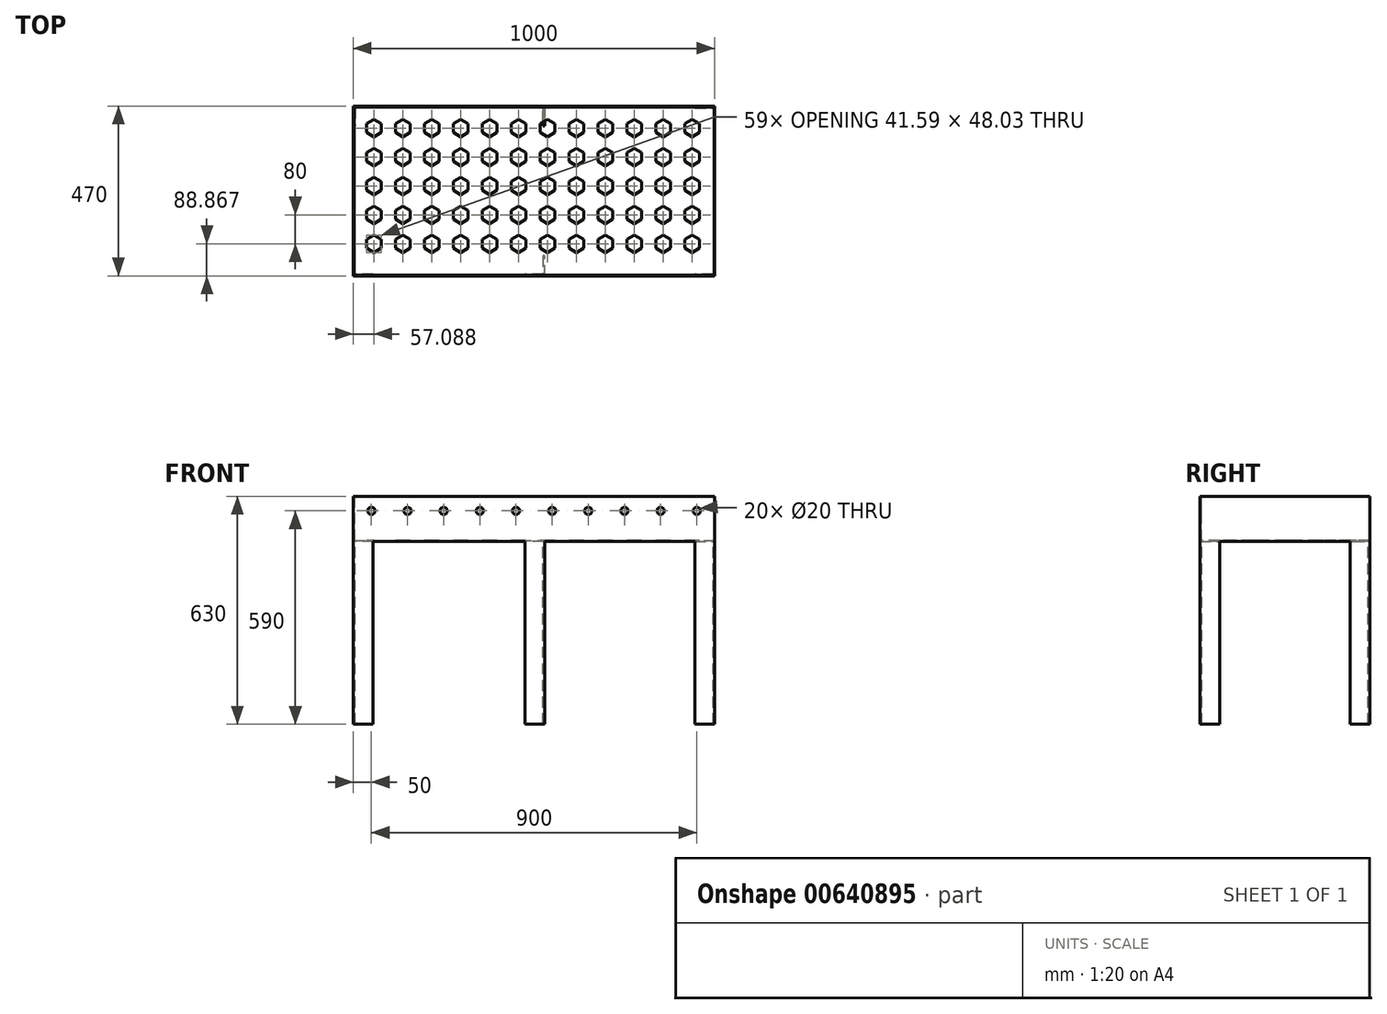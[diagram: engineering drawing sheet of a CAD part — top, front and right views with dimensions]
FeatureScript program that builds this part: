
annotation { "Feature Type Name" : "Feature", "Feature Type Description" : "" }
export const myFeature = defineFeature(function(context is Context, id is Id, definition is map)
    precondition{}
    {
        {
            var Q0;
            Q0=qCreatedBy(makeId("Top.planeOp"),FACE);
            cPlane(context, id + "F0", {"entities" : qUnion([Q0]), "cplaneType" : CPlaneType.OFFSET, "offset" : 505 * mm, "width" : 152.4 * mm, "height" : 152.4 * mm});
        }
        {
            var Q0;
            Q0=qCreatedBy(id+"F0.planeOp",FACE);
            var sketch = newSketch(context, id + "F1", { "sketchPlane" : qUnion([Q0])});
            skLineSegment(sketch, "E0", {"start": v(0, 1050.52) * mm, "end": v(0, -1050.52) * mm, "construction": true});
            skLineSegment(sketch, "E1", {"start": v(-920.74, 0) * mm, "end": v(994.2, 0) * mm, "construction": true});
            skLineSegment(sketch, "E2.bottom", {"start": v(-500, 235) * mm, "end": v(500, 235) * mm});
            skLineSegment(sketch, "E2.top", {"start": v(-500, -235) * mm, "end": v(500, -235) * mm});
            skLineSegment(sketch, "E2.left", {"start": v(-500, 235) * mm, "end": v(-500, -235) * mm});
            skLineSegment(sketch, "E2.right", {"start": v(500, 235) * mm, "end": v(500, -235) * mm});
            skSolve(sketch);
        }
        {
            var Q0;
            Q0=makeQuery(id+"F1.imprint","IMPRINT",FACE,{"disambiguationData":[TD([[makeQuery(id+"F1.imprint","IMPRINT",EDGE,{"derivedFrom":sQuery(id+"F1.wireOp",EDGE,"E2.bottom")}),-1.0]])]});
            extrude(context, id + "F2", {"entities" : qUnion([Q0]), "depth" : 125 * mm, "offsetDistance" : 25.4 * mm});
        }
        {
            var Q0;
            Q0=makeQuery(id+"F2.opExtrude","CAP_FACE",FACE,{"disambiguationData":[OSD([sQuery(id+"F1.wireOp",EDGE,"E2.bottom"),sQuery(id+"F1.wireOp",EDGE,"E2.top"),sQuery(id+"F1.wireOp",EDGE,"E2.left"),sQuery(id+"F1.wireOp",EDGE,"E2.right")])],"isStart":false});
            shell(context, id + "F3", {"entities" : qUnion([Q0]), "thickness" : 2.54 * mm});
        }
        {
            var Q0;
            Q0=makeQuery(id+"F2.opExtrude","CAP_FACE",FACE,{"disambiguationData":[OSD([sQuery(id+"F1.wireOp",EDGE,"E2.bottom"),sQuery(id+"F1.wireOp",EDGE,"E2.top"),sQuery(id+"F1.wireOp",EDGE,"E2.left"),sQuery(id+"F1.wireOp",EDGE,"E2.right")])],"isStart":true});
            var sketch = newSketch(context, id + "F4", { "sketchPlane" : qUnion([Q0])});
            skLineSegment(sketch, "E3", {"start": v(445, 235) * mm, "end": v(500, 235) * mm});
            skLineSegment(sketch, "E4", {"start": v(500, 235) * mm, "end": v(500, 180) * mm});
            skLineSegment(sketch, "E5", {"start": v(500, 180) * mm, "end": v(495, 180) * mm});
            skLineSegment(sketch, "E6", {"start": v(495, 180) * mm, "end": v(495, 230) * mm});
            skLineSegment(sketch, "E7", {"start": v(495, 230) * mm, "end": v(445, 230) * mm});
            skLineSegment(sketch, "E8", {"start": v(445, 230) * mm, "end": v(445, 235) * mm});
            skLineSegment(sketch, "E9", {"start": v(500, -180) * mm, "end": v(500, -235) * mm});
            skLineSegment(sketch, "E10", {"start": v(500, -235) * mm, "end": v(445, -235) * mm});
            skLineSegment(sketch, "E11", {"start": v(445, -235) * mm, "end": v(445, -230) * mm});
            skLineSegment(sketch, "E12", {"start": v(445, -230) * mm, "end": v(495, -230) * mm});
            skLineSegment(sketch, "E13", {"start": v(495, -230) * mm, "end": v(495, -180) * mm});
            skLineSegment(sketch, "E14", {"start": v(495, -180) * mm, "end": v(500, -180) * mm});
            skLineSegment(sketch, "E15", {"start": v(0, 297.82) * mm, "end": v(0, -372.57) * mm, "construction": true});
            skLineSegment(sketch, "E16", {"start": v(-25, 235) * mm, "end": v(30, 235) * mm});
            skLineSegment(sketch, "E17", {"start": v(30, 235) * mm, "end": v(30, 180) * mm});
            skLineSegment(sketch, "E18", {"start": v(30, 180) * mm, "end": v(25, 180) * mm});
            skLineSegment(sketch, "E19", {"start": v(25, 180) * mm, "end": v(25, 230) * mm});
            skLineSegment(sketch, "E20", {"start": v(25, 230) * mm, "end": v(-25, 230) * mm});
            skLineSegment(sketch, "E21", {"start": v(-25, 230) * mm, "end": v(-25, 235) * mm});
            skLineSegment(sketch, "E22", {"start": v(-25, -235) * mm, "end": v(30, -235) * mm});
            skLineSegment(sketch, "E23", {"start": v(30, -235) * mm, "end": v(30, -180) * mm});
            skLineSegment(sketch, "E24", {"start": v(30, -180) * mm, "end": v(25, -180) * mm});
            skLineSegment(sketch, "E25", {"start": v(25, -180) * mm, "end": v(25, -230) * mm});
            skLineSegment(sketch, "E26", {"start": v(25, -230) * mm, "end": v(-25, -230) * mm});
            skLineSegment(sketch, "E27", {"start": v(-25, -230) * mm, "end": v(-25, -235) * mm});
            skLineSegment(sketch, "E28", {"start": v(-500, 180) * mm, "end": v(-500, 235) * mm});
            skLineSegment(sketch, "E29", {"start": v(-500, 235) * mm, "end": v(-445, 235) * mm});
            skLineSegment(sketch, "E30", {"start": v(-445, 235) * mm, "end": v(-445, 230) * mm});
            skLineSegment(sketch, "E31", {"start": v(-445, 230) * mm, "end": v(-495, 230) * mm});
            skLineSegment(sketch, "E32", {"start": v(-495, 230) * mm, "end": v(-495, 180) * mm});
            skLineSegment(sketch, "E33", {"start": v(-495, 180) * mm, "end": v(-500, 180) * mm});
            skLineSegment(sketch, "E34", {"start": v(-500, -180) * mm, "end": v(-500, -235) * mm});
            skLineSegment(sketch, "E35", {"start": v(-500, -235) * mm, "end": v(-445, -235) * mm});
            skLineSegment(sketch, "E36", {"start": v(-445, -235) * mm, "end": v(-445, -230) * mm});
            skLineSegment(sketch, "E37", {"start": v(-445, -230) * mm, "end": v(-495, -230) * mm});
            skLineSegment(sketch, "E38", {"start": v(-495, -230) * mm, "end": v(-495, -180) * mm});
            skLineSegment(sketch, "E39", {"start": v(-495, -180) * mm, "end": v(-500, -180) * mm});
            skSolve(sketch);
        }
        {
            var Q0;
            Q0 = qSketchRegion(id + "F4", true);
            var Q1;
            Q1=qCreatedBy(makeId("Top.planeOp"),FACE);
            extrude(context, id + "F5", {"entities" : qUnion([Q0]), "operationType" : NewBodyOperationType.ADD, "endBound" : BoundingType.UP_TO_SURFACE, "depth" : 25.4 * mm, "endBoundEntityFace" : qUnion([Q1]), "offsetDistance" : 25.4 * mm});
        }
        {
            var Q0;
            Q0=makeQuery(id+"F5.boolean.opBoolean","MERGE",FACE,{"derivedFrom":[makeQuery(id+"F2.opExtrude","SWEPT_FACE",FACE,{"disambiguationData":[OSD([sQuery(id+"F1.wireOp",EDGE,"E2.top")])]}),makeQuery(id+"F5.opExtrude","SWEPT_FACE",FACE,{"disambiguationData":[OSD([sQuery(id+"F4.wireOp",EDGE,"E3")])]}),makeQuery(id+"F5.opExtrude","SWEPT_FACE",FACE,{"disambiguationData":[OSD([sQuery(id+"F4.wireOp",EDGE,"E16")])]}),makeQuery(id+"F5.opExtrude","SWEPT_FACE",FACE,{"disambiguationData":[OSD([sQuery(id+"F4.wireOp",EDGE,"E29")])]})]});
            var sketch = newSketch(context, id + "F6", { "sketchPlane" : qUnion([Q0])});
            skCircle(sketch, "E40", {"center": v(-450, 590) * mm, "radius": 10 * mm});
            skLineSegment(sketch, "E41", {"start": v(500, 590) * mm, "end": v(-1105.83, 590) * mm, "construction": true});
            skLineSegment(sketch, "E42", {"start": v(0, 770.39) * mm, "end": v(0, 138.73) * mm, "construction": true});
            skCircle(sketch, "E43.1.0.0", {"center": v(-350, 590) * mm, "radius": 10 * mm});
            skLineSegment(sketch, "E43.1.0.1", {"start": v(600, 590) * mm, "end": v(-1005.83, 590) * mm, "construction": true});
            skCircle(sketch, "E43.2.0.0", {"center": v(-250, 590) * mm, "radius": 10 * mm});
            skLineSegment(sketch, "E43.2.0.1", {"start": v(700, 590) * mm, "end": v(-905.83, 590) * mm, "construction": true});
            skCircle(sketch, "E43.3.0.0", {"center": v(-150, 590) * mm, "radius": 10 * mm});
            skLineSegment(sketch, "E43.3.0.1", {"start": v(800, 590) * mm, "end": v(-805.83, 590) * mm, "construction": true});
            skCircle(sketch, "E43.4.0.0", {"center": v(-50, 590) * mm, "radius": 10 * mm});
            skLineSegment(sketch, "E43.4.0.1", {"start": v(900, 590) * mm, "end": v(-705.83, 590) * mm, "construction": true});
            skLineSegment(sketch, "E43.direction1", {"start": v(-450, 590) * mm, "end": v(-350, 590) * mm, "construction": true});
            skCircle(sketch, "E44.0.5.0", {"center": v(50, 590) * mm, "radius": 10 * mm});
            skLineSegment(sketch, "E44.2.5.0", {"start": v(1000, 590) * mm, "end": v(-605.83, 590) * mm, "construction": true});
            skCircle(sketch, "E44.0.6.0", {"center": v(150, 590) * mm, "radius": 10 * mm});
            skLineSegment(sketch, "E44.2.6.0", {"start": v(1100, 590) * mm, "end": v(-505.83, 590) * mm, "construction": true});
            skCircle(sketch, "E44.0.7.0", {"center": v(250, 590) * mm, "radius": 10 * mm});
            skLineSegment(sketch, "E44.2.7.0", {"start": v(1200, 590) * mm, "end": v(-405.83, 590) * mm, "construction": true});
            skCircle(sketch, "E44.0.8.0", {"center": v(350, 590) * mm, "radius": 10 * mm});
            skLineSegment(sketch, "E44.2.8.0", {"start": v(1300, 590) * mm, "end": v(-305.83, 590) * mm, "construction": true});
            skCircle(sketch, "E44.0.9.0", {"center": v(450, 590) * mm, "radius": 10 * mm});
            skLineSegment(sketch, "E44.2.9.0", {"start": v(1400, 590) * mm, "end": v(-205.83, 590) * mm, "construction": true});
            skCircle(sketch, "E45.0.10.0", {"center": v(550, 590) * mm, "radius": 10 * mm});
            skLineSegment(sketch, "E45.2.10.0", {"start": v(1500, 590) * mm, "end": v(-105.83, 590) * mm, "construction": true});
            skCircle(sketch, "E45.0.11.0", {"center": v(650, 590) * mm, "radius": 10 * mm});
            skLineSegment(sketch, "E45.2.11.0", {"start": v(1600, 590) * mm, "end": v(-5.83, 590) * mm, "construction": true});
            skCircle(sketch, "E45.0.12.0", {"center": v(750, 590) * mm, "radius": 10 * mm});
            skLineSegment(sketch, "E45.2.12.0", {"start": v(1700, 590) * mm, "end": v(94.17, 590) * mm, "construction": true});
            skCircle(sketch, "E45.0.13.0", {"center": v(850, 590) * mm, "radius": 10 * mm});
            skLineSegment(sketch, "E45.2.13.0", {"start": v(1800, 590) * mm, "end": v(194.17, 590) * mm, "construction": true});
            skCircle(sketch, "E45.0.14.0", {"center": v(950, 590) * mm, "radius": 10 * mm});
            skLineSegment(sketch, "E45.2.14.0", {"start": v(1900, 590) * mm, "end": v(294.17, 590) * mm, "construction": true});
            skCircle(sketch, "E46.0.15.0", {"center": v(1050, 590) * mm, "radius": 10 * mm});
            skLineSegment(sketch, "E46.2.15.0", {"start": v(2000, 590) * mm, "end": v(394.17, 590) * mm, "construction": true});
            skCircle(sketch, "E46.0.16.0", {"center": v(1150, 590) * mm, "radius": 10 * mm});
            skLineSegment(sketch, "E46.2.16.0", {"start": v(2100, 590) * mm, "end": v(494.17, 590) * mm, "construction": true});
            skCircle(sketch, "E47.0.17.0", {"center": v(1250, 590) * mm, "radius": 10 * mm});
            skLineSegment(sketch, "E47.2.17.0", {"start": v(2200, 590) * mm, "end": v(594.17, 590) * mm, "construction": true});
            skCircle(sketch, "E47.0.18.0", {"center": v(1350, 590) * mm, "radius": 10 * mm});
            skLineSegment(sketch, "E47.2.18.0", {"start": v(2300, 590) * mm, "end": v(694.17, 590) * mm, "construction": true});
            skCircle(sketch, "E47.0.19.0", {"center": v(1450, 590) * mm, "radius": 10 * mm});
            skLineSegment(sketch, "E47.2.19.0", {"start": v(2400, 590) * mm, "end": v(794.17, 590) * mm, "construction": true});
            skSolve(sketch);
        }
        {
            var Q0;
            Q0 = qSketchRegion(id + "F6", true);
            var Q1;
            Q1=makeQuery(id+"F5.boolean.opBoolean","MERGE",FACE,{"derivedFrom":[makeQuery(id+"F2.opExtrude","SWEPT_FACE",FACE,{"disambiguationData":[OSD([sQuery(id+"F1.wireOp",EDGE,"E2.bottom")])]}),makeQuery(id+"F5.opExtrude","SWEPT_FACE",FACE,{"disambiguationData":[OSD([sQuery(id+"F4.wireOp",EDGE,"E10")])]}),makeQuery(id+"F5.opExtrude","SWEPT_FACE",FACE,{"disambiguationData":[OSD([sQuery(id+"F4.wireOp",EDGE,"E22")])]}),makeQuery(id+"F5.opExtrude","SWEPT_FACE",FACE,{"disambiguationData":[OSD([sQuery(id+"F4.wireOp",EDGE,"E35")])]})]});
            extrude(context, id + "F7", {"entities" : qUnion([Q0]), "operationType" : NewBodyOperationType.REMOVE, "endBound" : BoundingType.UP_TO_SURFACE, "oppositeDirection" : true, "depth" : 25.4 * mm, "endBoundEntityFace" : qUnion([Q1]), "offsetDistance" : 25.4 * mm});
        }
        {
            var Q0;
            Q0=makeQuery(id+"F3.opShell","OFFSET_FACE",FACE,{"disambiguationData":[OSD([sQuery(id+"F1.wireOp",EDGE,"E2.bottom"),sQuery(id+"F1.wireOp",EDGE,"E2.top"),sQuery(id+"F1.wireOp",EDGE,"E2.left"),sQuery(id+"F1.wireOp",EDGE,"E2.right")])]});
            var sketch = newSketch(context, id + "F8", { "sketchPlane" : qUnion([Q0])});
            skCircle(sketch, "E48.cCircle", {"center": v(-442.91, 173.87) * mm, "radius": 20.8 * mm, "construction": true});
            skLineSegment(sketch, "E48.0", {"start": v(-422.12, 185.87) * mm, "end": v(-422.12, 161.86) * mm});
            skLineSegment(sketch, "E48.1", {"start": v(-422.12, 161.86) * mm, "end": v(-442.91, 149.85) * mm});
            skLineSegment(sketch, "E48.2", {"start": v(-442.91, 149.85) * mm, "end": v(-463.7, 161.86) * mm});
            skLineSegment(sketch, "E48.3", {"start": v(-463.7, 161.86) * mm, "end": v(-463.7, 185.87) * mm});
            skLineSegment(sketch, "E48.4", {"start": v(-463.7, 185.87) * mm, "end": v(-442.91, 197.88) * mm});
            skLineSegment(sketch, "E48.5", {"start": v(-442.91, 197.88) * mm, "end": v(-422.12, 185.87) * mm});
            skPoint(sketch, "E48.0.midPoint", {"position": v(-422.12, 173.87) * mm});
            skLineSegment(sketch, "E49.0.1.0", {"start": v(-422.12, 81.86) * mm, "end": v(-442.91, 69.85) * mm});
            skLineSegment(sketch, "E49.0.1.1", {"start": v(-422.12, 105.87) * mm, "end": v(-422.12, 81.86) * mm});
            skLineSegment(sketch, "E49.0.1.2", {"start": v(-442.91, 117.88) * mm, "end": v(-422.12, 105.87) * mm});
            skLineSegment(sketch, "E49.0.1.3", {"start": v(-463.7, 105.87) * mm, "end": v(-442.91, 117.88) * mm});
            skLineSegment(sketch, "E49.0.1.4", {"start": v(-463.7, 81.86) * mm, "end": v(-463.7, 105.87) * mm});
            skLineSegment(sketch, "E49.0.1.5", {"start": v(-442.91, 69.85) * mm, "end": v(-463.7, 81.86) * mm});
            skLineSegment(sketch, "E49.0.2.0", {"start": v(-422.12, 1.86) * mm, "end": v(-442.91, -10.15) * mm});
            skLineSegment(sketch, "E49.0.2.1", {"start": v(-422.12, 25.87) * mm, "end": v(-422.12, 1.86) * mm});
            skLineSegment(sketch, "E49.0.2.2", {"start": v(-442.91, 37.88) * mm, "end": v(-422.12, 25.87) * mm});
            skLineSegment(sketch, "E49.0.2.3", {"start": v(-463.7, 25.87) * mm, "end": v(-442.91, 37.88) * mm});
            skLineSegment(sketch, "E49.0.2.4", {"start": v(-463.7, 1.86) * mm, "end": v(-463.7, 25.87) * mm});
            skLineSegment(sketch, "E49.0.2.5", {"start": v(-442.91, -10.15) * mm, "end": v(-463.7, 1.86) * mm});
            skLineSegment(sketch, "E49.0.3.0", {"start": v(-422.12, -78.14) * mm, "end": v(-442.91, -90.15) * mm});
            skLineSegment(sketch, "E49.0.3.1", {"start": v(-422.12, -54.13) * mm, "end": v(-422.12, -78.14) * mm});
            skLineSegment(sketch, "E49.0.3.2", {"start": v(-442.91, -42.12) * mm, "end": v(-422.12, -54.13) * mm});
            skLineSegment(sketch, "E49.0.3.3", {"start": v(-463.7, -54.13) * mm, "end": v(-442.91, -42.12) * mm});
            skLineSegment(sketch, "E49.0.3.4", {"start": v(-463.7, -78.14) * mm, "end": v(-463.7, -54.13) * mm});
            skLineSegment(sketch, "E49.0.3.5", {"start": v(-442.91, -90.15) * mm, "end": v(-463.7, -78.14) * mm});
            skLineSegment(sketch, "E49.0.4.0", {"start": v(-422.12, -158.14) * mm, "end": v(-442.91, -170.15) * mm});
            skLineSegment(sketch, "E49.0.4.1", {"start": v(-422.12, -134.13) * mm, "end": v(-422.12, -158.14) * mm});
            skLineSegment(sketch, "E49.0.4.2", {"start": v(-442.91, -122.12) * mm, "end": v(-422.12, -134.13) * mm});
            skLineSegment(sketch, "E49.0.4.3", {"start": v(-463.7, -134.13) * mm, "end": v(-442.91, -122.12) * mm});
            skLineSegment(sketch, "E49.0.4.4", {"start": v(-463.7, -158.14) * mm, "end": v(-463.7, -134.13) * mm});
            skLineSegment(sketch, "E49.0.4.5", {"start": v(-442.91, -170.15) * mm, "end": v(-463.7, -158.14) * mm});
            skLineSegment(sketch, "E49.1.0.0", {"start": v(-342.12, 161.86) * mm, "end": v(-362.91, 149.85) * mm});
            skLineSegment(sketch, "E49.1.0.1", {"start": v(-342.12, 185.87) * mm, "end": v(-342.12, 161.86) * mm});
            skLineSegment(sketch, "E49.1.0.2", {"start": v(-362.91, 197.88) * mm, "end": v(-342.12, 185.87) * mm});
            skLineSegment(sketch, "E49.1.0.3", {"start": v(-383.7, 185.87) * mm, "end": v(-362.91, 197.88) * mm});
            skLineSegment(sketch, "E49.1.0.4", {"start": v(-383.7, 161.86) * mm, "end": v(-383.7, 185.87) * mm});
            skLineSegment(sketch, "E49.1.0.5", {"start": v(-362.91, 149.85) * mm, "end": v(-383.7, 161.86) * mm});
            skLineSegment(sketch, "E49.1.1.0", {"start": v(-342.12, 81.86) * mm, "end": v(-362.91, 69.85) * mm});
            skLineSegment(sketch, "E49.1.1.1", {"start": v(-342.12, 105.87) * mm, "end": v(-342.12, 81.86) * mm});
            skLineSegment(sketch, "E49.1.1.2", {"start": v(-362.91, 117.88) * mm, "end": v(-342.12, 105.87) * mm});
            skLineSegment(sketch, "E49.1.1.3", {"start": v(-383.7, 105.87) * mm, "end": v(-362.91, 117.88) * mm});
            skLineSegment(sketch, "E49.1.1.4", {"start": v(-383.7, 81.86) * mm, "end": v(-383.7, 105.87) * mm});
            skLineSegment(sketch, "E49.1.1.5", {"start": v(-362.91, 69.85) * mm, "end": v(-383.7, 81.86) * mm});
            skLineSegment(sketch, "E49.1.2.0", {"start": v(-342.12, 1.86) * mm, "end": v(-362.91, -10.15) * mm});
            skLineSegment(sketch, "E49.1.2.1", {"start": v(-342.12, 25.87) * mm, "end": v(-342.12, 1.86) * mm});
            skLineSegment(sketch, "E49.1.2.2", {"start": v(-362.91, 37.88) * mm, "end": v(-342.12, 25.87) * mm});
            skLineSegment(sketch, "E49.1.2.3", {"start": v(-383.7, 25.87) * mm, "end": v(-362.91, 37.88) * mm});
            skLineSegment(sketch, "E49.1.2.4", {"start": v(-383.7, 1.86) * mm, "end": v(-383.7, 25.87) * mm});
            skLineSegment(sketch, "E49.1.2.5", {"start": v(-362.91, -10.15) * mm, "end": v(-383.7, 1.86) * mm});
            skLineSegment(sketch, "E49.1.3.0", {"start": v(-342.12, -78.14) * mm, "end": v(-362.91, -90.15) * mm});
            skLineSegment(sketch, "E49.1.3.1", {"start": v(-342.12, -54.13) * mm, "end": v(-342.12, -78.14) * mm});
            skLineSegment(sketch, "E49.1.3.2", {"start": v(-362.91, -42.12) * mm, "end": v(-342.12, -54.13) * mm});
            skLineSegment(sketch, "E49.1.3.3", {"start": v(-383.7, -54.13) * mm, "end": v(-362.91, -42.12) * mm});
            skLineSegment(sketch, "E49.1.3.4", {"start": v(-383.7, -78.14) * mm, "end": v(-383.7, -54.13) * mm});
            skLineSegment(sketch, "E49.1.3.5", {"start": v(-362.91, -90.15) * mm, "end": v(-383.7, -78.14) * mm});
            skLineSegment(sketch, "E49.1.4.0", {"start": v(-342.12, -158.14) * mm, "end": v(-362.91, -170.15) * mm});
            skLineSegment(sketch, "E49.1.4.1", {"start": v(-342.12, -134.13) * mm, "end": v(-342.12, -158.14) * mm});
            skLineSegment(sketch, "E49.1.4.2", {"start": v(-362.91, -122.12) * mm, "end": v(-342.12, -134.13) * mm});
            skLineSegment(sketch, "E49.1.4.3", {"start": v(-383.7, -134.13) * mm, "end": v(-362.91, -122.12) * mm});
            skLineSegment(sketch, "E49.1.4.4", {"start": v(-383.7, -158.14) * mm, "end": v(-383.7, -134.13) * mm});
            skLineSegment(sketch, "E49.1.4.5", {"start": v(-362.91, -170.15) * mm, "end": v(-383.7, -158.14) * mm});
            skLineSegment(sketch, "E49.2.0.0", {"start": v(-262.12, 161.86) * mm, "end": v(-282.91, 149.85) * mm});
            skLineSegment(sketch, "E49.2.0.1", {"start": v(-262.12, 185.87) * mm, "end": v(-262.12, 161.86) * mm});
            skLineSegment(sketch, "E49.2.0.2", {"start": v(-282.91, 197.88) * mm, "end": v(-262.12, 185.87) * mm});
            skLineSegment(sketch, "E49.2.0.3", {"start": v(-303.7, 185.87) * mm, "end": v(-282.91, 197.88) * mm});
            skLineSegment(sketch, "E49.2.0.4", {"start": v(-303.7, 161.86) * mm, "end": v(-303.7, 185.87) * mm});
            skLineSegment(sketch, "E49.2.0.5", {"start": v(-282.91, 149.85) * mm, "end": v(-303.7, 161.86) * mm});
            skLineSegment(sketch, "E49.2.1.0", {"start": v(-262.12, 81.86) * mm, "end": v(-282.91, 69.85) * mm});
            skLineSegment(sketch, "E49.2.1.1", {"start": v(-262.12, 105.87) * mm, "end": v(-262.12, 81.86) * mm});
            skLineSegment(sketch, "E49.2.1.2", {"start": v(-282.91, 117.88) * mm, "end": v(-262.12, 105.87) * mm});
            skLineSegment(sketch, "E49.2.1.3", {"start": v(-303.7, 105.87) * mm, "end": v(-282.91, 117.88) * mm});
            skLineSegment(sketch, "E49.2.1.4", {"start": v(-303.7, 81.86) * mm, "end": v(-303.7, 105.87) * mm});
            skLineSegment(sketch, "E49.2.1.5", {"start": v(-282.91, 69.85) * mm, "end": v(-303.7, 81.86) * mm});
            skLineSegment(sketch, "E49.2.2.0", {"start": v(-262.12, 1.86) * mm, "end": v(-282.91, -10.15) * mm});
            skLineSegment(sketch, "E49.2.2.1", {"start": v(-262.12, 25.87) * mm, "end": v(-262.12, 1.86) * mm});
            skLineSegment(sketch, "E49.2.2.2", {"start": v(-282.91, 37.88) * mm, "end": v(-262.12, 25.87) * mm});
            skLineSegment(sketch, "E49.2.2.3", {"start": v(-303.7, 25.87) * mm, "end": v(-282.91, 37.88) * mm});
            skLineSegment(sketch, "E49.2.2.4", {"start": v(-303.7, 1.86) * mm, "end": v(-303.7, 25.87) * mm});
            skLineSegment(sketch, "E49.2.2.5", {"start": v(-282.91, -10.15) * mm, "end": v(-303.7, 1.86) * mm});
            skLineSegment(sketch, "E49.2.3.0", {"start": v(-262.12, -78.14) * mm, "end": v(-282.91, -90.15) * mm});
            skLineSegment(sketch, "E49.2.3.1", {"start": v(-262.12, -54.13) * mm, "end": v(-262.12, -78.14) * mm});
            skLineSegment(sketch, "E49.2.3.2", {"start": v(-282.91, -42.12) * mm, "end": v(-262.12, -54.13) * mm});
            skLineSegment(sketch, "E49.2.3.3", {"start": v(-303.7, -54.13) * mm, "end": v(-282.91, -42.12) * mm});
            skLineSegment(sketch, "E49.2.3.4", {"start": v(-303.7, -78.14) * mm, "end": v(-303.7, -54.13) * mm});
            skLineSegment(sketch, "E49.2.3.5", {"start": v(-282.91, -90.15) * mm, "end": v(-303.7, -78.14) * mm});
            skLineSegment(sketch, "E49.2.4.0", {"start": v(-262.12, -158.14) * mm, "end": v(-282.91, -170.15) * mm});
            skLineSegment(sketch, "E49.2.4.1", {"start": v(-262.12, -134.13) * mm, "end": v(-262.12, -158.14) * mm});
            skLineSegment(sketch, "E49.2.4.2", {"start": v(-282.91, -122.12) * mm, "end": v(-262.12, -134.13) * mm});
            skLineSegment(sketch, "E49.2.4.3", {"start": v(-303.7, -134.13) * mm, "end": v(-282.91, -122.12) * mm});
            skLineSegment(sketch, "E49.2.4.4", {"start": v(-303.7, -158.14) * mm, "end": v(-303.7, -134.13) * mm});
            skLineSegment(sketch, "E49.2.4.5", {"start": v(-282.91, -170.15) * mm, "end": v(-303.7, -158.14) * mm});
            skLineSegment(sketch, "E49.3.0.0", {"start": v(-182.12, 161.86) * mm, "end": v(-202.91, 149.85) * mm});
            skLineSegment(sketch, "E49.3.0.1", {"start": v(-182.12, 185.87) * mm, "end": v(-182.12, 161.86) * mm});
            skLineSegment(sketch, "E49.3.0.2", {"start": v(-202.91, 197.88) * mm, "end": v(-182.12, 185.87) * mm});
            skLineSegment(sketch, "E49.3.0.3", {"start": v(-223.7, 185.87) * mm, "end": v(-202.91, 197.88) * mm});
            skLineSegment(sketch, "E49.3.0.4", {"start": v(-223.7, 161.86) * mm, "end": v(-223.7, 185.87) * mm});
            skLineSegment(sketch, "E49.3.0.5", {"start": v(-202.91, 149.85) * mm, "end": v(-223.7, 161.86) * mm});
            skLineSegment(sketch, "E49.3.1.0", {"start": v(-182.12, 81.86) * mm, "end": v(-202.91, 69.85) * mm});
            skLineSegment(sketch, "E49.3.1.1", {"start": v(-182.12, 105.87) * mm, "end": v(-182.12, 81.86) * mm});
            skLineSegment(sketch, "E49.3.1.2", {"start": v(-202.91, 117.88) * mm, "end": v(-182.12, 105.87) * mm});
            skLineSegment(sketch, "E49.3.1.3", {"start": v(-223.7, 105.87) * mm, "end": v(-202.91, 117.88) * mm});
            skLineSegment(sketch, "E49.3.1.4", {"start": v(-223.7, 81.86) * mm, "end": v(-223.7, 105.87) * mm});
            skLineSegment(sketch, "E49.3.1.5", {"start": v(-202.91, 69.85) * mm, "end": v(-223.7, 81.86) * mm});
            skLineSegment(sketch, "E49.3.2.0", {"start": v(-182.12, 1.86) * mm, "end": v(-202.91, -10.15) * mm});
            skLineSegment(sketch, "E49.3.2.1", {"start": v(-182.12, 25.87) * mm, "end": v(-182.12, 1.86) * mm});
            skLineSegment(sketch, "E49.3.2.2", {"start": v(-202.91, 37.88) * mm, "end": v(-182.12, 25.87) * mm});
            skLineSegment(sketch, "E49.3.2.3", {"start": v(-223.7, 25.87) * mm, "end": v(-202.91, 37.88) * mm});
            skLineSegment(sketch, "E49.3.2.4", {"start": v(-223.7, 1.86) * mm, "end": v(-223.7, 25.87) * mm});
            skLineSegment(sketch, "E49.3.2.5", {"start": v(-202.91, -10.15) * mm, "end": v(-223.7, 1.86) * mm});
            skLineSegment(sketch, "E49.3.3.0", {"start": v(-182.12, -78.14) * mm, "end": v(-202.91, -90.15) * mm});
            skLineSegment(sketch, "E49.3.3.1", {"start": v(-182.12, -54.13) * mm, "end": v(-182.12, -78.14) * mm});
            skLineSegment(sketch, "E49.3.3.2", {"start": v(-202.91, -42.12) * mm, "end": v(-182.12, -54.13) * mm});
            skLineSegment(sketch, "E49.3.3.3", {"start": v(-223.7, -54.13) * mm, "end": v(-202.91, -42.12) * mm});
            skLineSegment(sketch, "E49.3.3.4", {"start": v(-223.7, -78.14) * mm, "end": v(-223.7, -54.13) * mm});
            skLineSegment(sketch, "E49.3.3.5", {"start": v(-202.91, -90.15) * mm, "end": v(-223.7, -78.14) * mm});
            skLineSegment(sketch, "E49.3.4.0", {"start": v(-182.12, -158.14) * mm, "end": v(-202.91, -170.15) * mm});
            skLineSegment(sketch, "E49.3.4.1", {"start": v(-182.12, -134.13) * mm, "end": v(-182.12, -158.14) * mm});
            skLineSegment(sketch, "E49.3.4.2", {"start": v(-202.91, -122.12) * mm, "end": v(-182.12, -134.13) * mm});
            skLineSegment(sketch, "E49.3.4.3", {"start": v(-223.7, -134.13) * mm, "end": v(-202.91, -122.12) * mm});
            skLineSegment(sketch, "E49.3.4.4", {"start": v(-223.7, -158.14) * mm, "end": v(-223.7, -134.13) * mm});
            skLineSegment(sketch, "E49.3.4.5", {"start": v(-202.91, -170.15) * mm, "end": v(-223.7, -158.14) * mm});
            skLineSegment(sketch, "E49.4.0.0", {"start": v(-102.12, 161.86) * mm, "end": v(-122.91, 149.85) * mm});
            skLineSegment(sketch, "E49.4.0.1", {"start": v(-102.12, 185.87) * mm, "end": v(-102.12, 161.86) * mm});
            skLineSegment(sketch, "E49.4.0.2", {"start": v(-122.91, 197.88) * mm, "end": v(-102.12, 185.87) * mm});
            skLineSegment(sketch, "E49.4.0.3", {"start": v(-143.7, 185.87) * mm, "end": v(-122.91, 197.88) * mm});
            skLineSegment(sketch, "E49.4.0.4", {"start": v(-143.7, 161.86) * mm, "end": v(-143.7, 185.87) * mm});
            skLineSegment(sketch, "E49.4.0.5", {"start": v(-122.91, 149.85) * mm, "end": v(-143.7, 161.86) * mm});
            skLineSegment(sketch, "E49.4.1.0", {"start": v(-102.12, 81.86) * mm, "end": v(-122.91, 69.85) * mm});
            skLineSegment(sketch, "E49.4.1.1", {"start": v(-102.12, 105.87) * mm, "end": v(-102.12, 81.86) * mm});
            skLineSegment(sketch, "E49.4.1.2", {"start": v(-122.91, 117.88) * mm, "end": v(-102.12, 105.87) * mm});
            skLineSegment(sketch, "E49.4.1.3", {"start": v(-143.7, 105.87) * mm, "end": v(-122.91, 117.88) * mm});
            skLineSegment(sketch, "E49.4.1.4", {"start": v(-143.7, 81.86) * mm, "end": v(-143.7, 105.87) * mm});
            skLineSegment(sketch, "E49.4.1.5", {"start": v(-122.91, 69.85) * mm, "end": v(-143.7, 81.86) * mm});
            skLineSegment(sketch, "E49.4.2.0", {"start": v(-102.12, 1.86) * mm, "end": v(-122.91, -10.15) * mm});
            skLineSegment(sketch, "E49.4.2.1", {"start": v(-102.12, 25.87) * mm, "end": v(-102.12, 1.86) * mm});
            skLineSegment(sketch, "E49.4.2.2", {"start": v(-122.91, 37.88) * mm, "end": v(-102.12, 25.87) * mm});
            skLineSegment(sketch, "E49.4.2.3", {"start": v(-143.7, 25.87) * mm, "end": v(-122.91, 37.88) * mm});
            skLineSegment(sketch, "E49.4.2.4", {"start": v(-143.7, 1.86) * mm, "end": v(-143.7, 25.87) * mm});
            skLineSegment(sketch, "E49.4.2.5", {"start": v(-122.91, -10.15) * mm, "end": v(-143.7, 1.86) * mm});
            skLineSegment(sketch, "E49.4.3.0", {"start": v(-102.12, -78.14) * mm, "end": v(-122.91, -90.15) * mm});
            skLineSegment(sketch, "E49.4.3.1", {"start": v(-102.12, -54.13) * mm, "end": v(-102.12, -78.14) * mm});
            skLineSegment(sketch, "E49.4.3.2", {"start": v(-122.91, -42.12) * mm, "end": v(-102.12, -54.13) * mm});
            skLineSegment(sketch, "E49.4.3.3", {"start": v(-143.7, -54.13) * mm, "end": v(-122.91, -42.12) * mm});
            skLineSegment(sketch, "E49.4.3.4", {"start": v(-143.7, -78.14) * mm, "end": v(-143.7, -54.13) * mm});
            skLineSegment(sketch, "E49.4.3.5", {"start": v(-122.91, -90.15) * mm, "end": v(-143.7, -78.14) * mm});
            skLineSegment(sketch, "E49.4.4.0", {"start": v(-102.12, -158.14) * mm, "end": v(-122.91, -170.15) * mm});
            skLineSegment(sketch, "E49.4.4.1", {"start": v(-102.12, -134.13) * mm, "end": v(-102.12, -158.14) * mm});
            skLineSegment(sketch, "E49.4.4.2", {"start": v(-122.91, -122.12) * mm, "end": v(-102.12, -134.13) * mm});
            skLineSegment(sketch, "E49.4.4.3", {"start": v(-143.7, -134.13) * mm, "end": v(-122.91, -122.12) * mm});
            skLineSegment(sketch, "E49.4.4.4", {"start": v(-143.7, -158.14) * mm, "end": v(-143.7, -134.13) * mm});
            skLineSegment(sketch, "E49.4.4.5", {"start": v(-122.91, -170.15) * mm, "end": v(-143.7, -158.14) * mm});
            skLineSegment(sketch, "E49.5.0.0", {"start": v(-22.12, 161.86) * mm, "end": v(-42.91, 149.85) * mm});
            skLineSegment(sketch, "E49.5.0.1", {"start": v(-22.12, 185.87) * mm, "end": v(-22.12, 161.86) * mm});
            skLineSegment(sketch, "E49.5.0.2", {"start": v(-42.91, 197.88) * mm, "end": v(-22.12, 185.87) * mm});
            skLineSegment(sketch, "E49.5.0.3", {"start": v(-63.7, 185.87) * mm, "end": v(-42.91, 197.88) * mm});
            skLineSegment(sketch, "E49.5.0.4", {"start": v(-63.7, 161.86) * mm, "end": v(-63.7, 185.87) * mm});
            skLineSegment(sketch, "E49.5.0.5", {"start": v(-42.91, 149.85) * mm, "end": v(-63.7, 161.86) * mm});
            skLineSegment(sketch, "E49.5.1.0", {"start": v(-22.12, 81.86) * mm, "end": v(-42.91, 69.85) * mm});
            skLineSegment(sketch, "E49.5.1.1", {"start": v(-22.12, 105.87) * mm, "end": v(-22.12, 81.86) * mm});
            skLineSegment(sketch, "E49.5.1.2", {"start": v(-42.91, 117.88) * mm, "end": v(-22.12, 105.87) * mm});
            skLineSegment(sketch, "E49.5.1.3", {"start": v(-63.7, 105.87) * mm, "end": v(-42.91, 117.88) * mm});
            skLineSegment(sketch, "E49.5.1.4", {"start": v(-63.7, 81.86) * mm, "end": v(-63.7, 105.87) * mm});
            skLineSegment(sketch, "E49.5.1.5", {"start": v(-42.91, 69.85) * mm, "end": v(-63.7, 81.86) * mm});
            skLineSegment(sketch, "E49.5.2.0", {"start": v(-22.12, 1.86) * mm, "end": v(-42.91, -10.15) * mm});
            skLineSegment(sketch, "E49.5.2.1", {"start": v(-22.12, 25.87) * mm, "end": v(-22.12, 1.86) * mm});
            skLineSegment(sketch, "E49.5.2.2", {"start": v(-42.91, 37.88) * mm, "end": v(-22.12, 25.87) * mm});
            skLineSegment(sketch, "E49.5.2.3", {"start": v(-63.7, 25.87) * mm, "end": v(-42.91, 37.88) * mm});
            skLineSegment(sketch, "E49.5.2.4", {"start": v(-63.7, 1.86) * mm, "end": v(-63.7, 25.87) * mm});
            skLineSegment(sketch, "E49.5.2.5", {"start": v(-42.91, -10.15) * mm, "end": v(-63.7, 1.86) * mm});
            skLineSegment(sketch, "E49.5.3.0", {"start": v(-22.12, -78.14) * mm, "end": v(-42.91, -90.15) * mm});
            skLineSegment(sketch, "E49.5.3.1", {"start": v(-22.12, -54.13) * mm, "end": v(-22.12, -78.14) * mm});
            skLineSegment(sketch, "E49.5.3.2", {"start": v(-42.91, -42.12) * mm, "end": v(-22.12, -54.13) * mm});
            skLineSegment(sketch, "E49.5.3.3", {"start": v(-63.7, -54.13) * mm, "end": v(-42.91, -42.12) * mm});
            skLineSegment(sketch, "E49.5.3.4", {"start": v(-63.7, -78.14) * mm, "end": v(-63.7, -54.13) * mm});
            skLineSegment(sketch, "E49.5.3.5", {"start": v(-42.91, -90.15) * mm, "end": v(-63.7, -78.14) * mm});
            skLineSegment(sketch, "E49.5.4.0", {"start": v(-22.12, -158.14) * mm, "end": v(-42.91, -170.15) * mm});
            skLineSegment(sketch, "E49.5.4.1", {"start": v(-22.12, -134.13) * mm, "end": v(-22.12, -158.14) * mm});
            skLineSegment(sketch, "E49.5.4.2", {"start": v(-42.91, -122.12) * mm, "end": v(-22.12, -134.13) * mm});
            skLineSegment(sketch, "E49.5.4.3", {"start": v(-63.7, -134.13) * mm, "end": v(-42.91, -122.12) * mm});
            skLineSegment(sketch, "E49.5.4.4", {"start": v(-63.7, -158.14) * mm, "end": v(-63.7, -134.13) * mm});
            skLineSegment(sketch, "E49.5.4.5", {"start": v(-42.91, -170.15) * mm, "end": v(-63.7, -158.14) * mm});
            skLineSegment(sketch, "E49.6.0.0", {"start": v(57.88, 161.86) * mm, "end": v(37.09, 149.85) * mm});
            skLineSegment(sketch, "E49.6.0.1", {"start": v(57.88, 185.87) * mm, "end": v(57.88, 161.86) * mm});
            skLineSegment(sketch, "E49.6.0.2", {"start": v(37.09, 197.88) * mm, "end": v(57.88, 185.87) * mm});
            skLineSegment(sketch, "E49.6.0.3", {"start": v(16.3, 185.87) * mm, "end": v(37.09, 197.88) * mm});
            skLineSegment(sketch, "E49.6.0.4", {"start": v(16.3, 161.86) * mm, "end": v(16.3, 185.87) * mm});
            skLineSegment(sketch, "E49.6.0.5", {"start": v(37.09, 149.85) * mm, "end": v(16.3, 161.86) * mm});
            skLineSegment(sketch, "E49.6.1.0", {"start": v(57.88, 81.86) * mm, "end": v(37.09, 69.85) * mm});
            skLineSegment(sketch, "E49.6.1.1", {"start": v(57.88, 105.87) * mm, "end": v(57.88, 81.86) * mm});
            skLineSegment(sketch, "E49.6.1.2", {"start": v(37.09, 117.88) * mm, "end": v(57.88, 105.87) * mm});
            skLineSegment(sketch, "E49.6.1.3", {"start": v(16.3, 105.87) * mm, "end": v(37.09, 117.88) * mm});
            skLineSegment(sketch, "E49.6.1.4", {"start": v(16.3, 81.86) * mm, "end": v(16.3, 105.87) * mm});
            skLineSegment(sketch, "E49.6.1.5", {"start": v(37.09, 69.85) * mm, "end": v(16.3, 81.86) * mm});
            skLineSegment(sketch, "E49.6.2.0", {"start": v(57.88, 1.86) * mm, "end": v(37.09, -10.15) * mm});
            skLineSegment(sketch, "E49.6.2.1", {"start": v(57.88, 25.87) * mm, "end": v(57.88, 1.86) * mm});
            skLineSegment(sketch, "E49.6.2.2", {"start": v(37.09, 37.88) * mm, "end": v(57.88, 25.87) * mm});
            skLineSegment(sketch, "E49.6.2.3", {"start": v(16.3, 25.87) * mm, "end": v(37.09, 37.88) * mm});
            skLineSegment(sketch, "E49.6.2.4", {"start": v(16.3, 1.86) * mm, "end": v(16.3, 25.87) * mm});
            skLineSegment(sketch, "E49.6.2.5", {"start": v(37.09, -10.15) * mm, "end": v(16.3, 1.86) * mm});
            skLineSegment(sketch, "E49.6.3.0", {"start": v(57.88, -78.14) * mm, "end": v(37.09, -90.15) * mm});
            skLineSegment(sketch, "E49.6.3.1", {"start": v(57.88, -54.13) * mm, "end": v(57.88, -78.14) * mm});
            skLineSegment(sketch, "E49.6.3.2", {"start": v(37.09, -42.12) * mm, "end": v(57.88, -54.13) * mm});
            skLineSegment(sketch, "E49.6.3.3", {"start": v(16.3, -54.13) * mm, "end": v(37.09, -42.12) * mm});
            skLineSegment(sketch, "E49.6.3.4", {"start": v(16.3, -78.14) * mm, "end": v(16.3, -54.13) * mm});
            skLineSegment(sketch, "E49.6.3.5", {"start": v(37.09, -90.15) * mm, "end": v(16.3, -78.14) * mm});
            skLineSegment(sketch, "E49.6.4.0", {"start": v(57.88, -158.14) * mm, "end": v(37.09, -170.15) * mm});
            skLineSegment(sketch, "E49.6.4.1", {"start": v(57.88, -134.13) * mm, "end": v(57.88, -158.14) * mm});
            skLineSegment(sketch, "E49.6.4.2", {"start": v(37.09, -122.12) * mm, "end": v(57.88, -134.13) * mm});
            skLineSegment(sketch, "E49.6.4.3", {"start": v(16.3, -134.13) * mm, "end": v(37.09, -122.12) * mm});
            skLineSegment(sketch, "E49.6.4.4", {"start": v(16.3, -158.14) * mm, "end": v(16.3, -134.13) * mm});
            skLineSegment(sketch, "E49.6.4.5", {"start": v(37.09, -170.15) * mm, "end": v(16.3, -158.14) * mm});
            skLineSegment(sketch, "E49.7.0.0", {"start": v(137.88, 161.86) * mm, "end": v(117.09, 149.85) * mm});
            skLineSegment(sketch, "E49.7.0.1", {"start": v(137.88, 185.87) * mm, "end": v(137.88, 161.86) * mm});
            skLineSegment(sketch, "E49.7.0.2", {"start": v(117.09, 197.88) * mm, "end": v(137.88, 185.87) * mm});
            skLineSegment(sketch, "E49.7.0.3", {"start": v(96.3, 185.87) * mm, "end": v(117.09, 197.88) * mm});
            skLineSegment(sketch, "E49.7.0.4", {"start": v(96.3, 161.86) * mm, "end": v(96.3, 185.87) * mm});
            skLineSegment(sketch, "E49.7.0.5", {"start": v(117.09, 149.85) * mm, "end": v(96.3, 161.86) * mm});
            skLineSegment(sketch, "E49.7.1.0", {"start": v(137.88, 81.86) * mm, "end": v(117.09, 69.85) * mm});
            skLineSegment(sketch, "E49.7.1.1", {"start": v(137.88, 105.87) * mm, "end": v(137.88, 81.86) * mm});
            skLineSegment(sketch, "E49.7.1.2", {"start": v(117.09, 117.88) * mm, "end": v(137.88, 105.87) * mm});
            skLineSegment(sketch, "E49.7.1.3", {"start": v(96.3, 105.87) * mm, "end": v(117.09, 117.88) * mm});
            skLineSegment(sketch, "E49.7.1.4", {"start": v(96.3, 81.86) * mm, "end": v(96.3, 105.87) * mm});
            skLineSegment(sketch, "E49.7.1.5", {"start": v(117.09, 69.85) * mm, "end": v(96.3, 81.86) * mm});
            skLineSegment(sketch, "E49.7.2.0", {"start": v(137.88, 1.86) * mm, "end": v(117.09, -10.15) * mm});
            skLineSegment(sketch, "E49.7.2.1", {"start": v(137.88, 25.87) * mm, "end": v(137.88, 1.86) * mm});
            skLineSegment(sketch, "E49.7.2.2", {"start": v(117.09, 37.88) * mm, "end": v(137.88, 25.87) * mm});
            skLineSegment(sketch, "E49.7.2.3", {"start": v(96.3, 25.87) * mm, "end": v(117.09, 37.88) * mm});
            skLineSegment(sketch, "E49.7.2.4", {"start": v(96.3, 1.86) * mm, "end": v(96.3, 25.87) * mm});
            skLineSegment(sketch, "E49.7.2.5", {"start": v(117.09, -10.15) * mm, "end": v(96.3, 1.86) * mm});
            skLineSegment(sketch, "E49.7.3.0", {"start": v(137.88, -78.14) * mm, "end": v(117.09, -90.15) * mm});
            skLineSegment(sketch, "E49.7.3.1", {"start": v(137.88, -54.13) * mm, "end": v(137.88, -78.14) * mm});
            skLineSegment(sketch, "E49.7.3.2", {"start": v(117.09, -42.12) * mm, "end": v(137.88, -54.13) * mm});
            skLineSegment(sketch, "E49.7.3.3", {"start": v(96.3, -54.13) * mm, "end": v(117.09, -42.12) * mm});
            skLineSegment(sketch, "E49.7.3.4", {"start": v(96.3, -78.14) * mm, "end": v(96.3, -54.13) * mm});
            skLineSegment(sketch, "E49.7.3.5", {"start": v(117.09, -90.15) * mm, "end": v(96.3, -78.14) * mm});
            skLineSegment(sketch, "E49.7.4.0", {"start": v(137.88, -158.14) * mm, "end": v(117.09, -170.15) * mm});
            skLineSegment(sketch, "E49.7.4.1", {"start": v(137.88, -134.13) * mm, "end": v(137.88, -158.14) * mm});
            skLineSegment(sketch, "E49.7.4.2", {"start": v(117.09, -122.12) * mm, "end": v(137.88, -134.13) * mm});
            skLineSegment(sketch, "E49.7.4.3", {"start": v(96.3, -134.13) * mm, "end": v(117.09, -122.12) * mm});
            skLineSegment(sketch, "E49.7.4.4", {"start": v(96.3, -158.14) * mm, "end": v(96.3, -134.13) * mm});
            skLineSegment(sketch, "E49.7.4.5", {"start": v(117.09, -170.15) * mm, "end": v(96.3, -158.14) * mm});
            skLineSegment(sketch, "E49.8.0.0", {"start": v(217.88, 161.86) * mm, "end": v(197.09, 149.85) * mm});
            skLineSegment(sketch, "E49.8.0.1", {"start": v(217.88, 185.87) * mm, "end": v(217.88, 161.86) * mm});
            skLineSegment(sketch, "E49.8.0.2", {"start": v(197.09, 197.88) * mm, "end": v(217.88, 185.87) * mm});
            skLineSegment(sketch, "E49.8.0.3", {"start": v(176.3, 185.87) * mm, "end": v(197.09, 197.88) * mm});
            skLineSegment(sketch, "E49.8.0.4", {"start": v(176.3, 161.86) * mm, "end": v(176.3, 185.87) * mm});
            skLineSegment(sketch, "E49.8.0.5", {"start": v(197.09, 149.85) * mm, "end": v(176.3, 161.86) * mm});
            skLineSegment(sketch, "E49.8.1.0", {"start": v(217.88, 81.86) * mm, "end": v(197.09, 69.85) * mm});
            skLineSegment(sketch, "E49.8.1.1", {"start": v(217.88, 105.87) * mm, "end": v(217.88, 81.86) * mm});
            skLineSegment(sketch, "E49.8.1.2", {"start": v(197.09, 117.88) * mm, "end": v(217.88, 105.87) * mm});
            skLineSegment(sketch, "E49.8.1.3", {"start": v(176.3, 105.87) * mm, "end": v(197.09, 117.88) * mm});
            skLineSegment(sketch, "E49.8.1.4", {"start": v(176.3, 81.86) * mm, "end": v(176.3, 105.87) * mm});
            skLineSegment(sketch, "E49.8.1.5", {"start": v(197.09, 69.85) * mm, "end": v(176.3, 81.86) * mm});
            skLineSegment(sketch, "E49.8.2.0", {"start": v(217.88, 1.86) * mm, "end": v(197.09, -10.15) * mm});
            skLineSegment(sketch, "E49.8.2.1", {"start": v(217.88, 25.87) * mm, "end": v(217.88, 1.86) * mm});
            skLineSegment(sketch, "E49.8.2.2", {"start": v(197.09, 37.88) * mm, "end": v(217.88, 25.87) * mm});
            skLineSegment(sketch, "E49.8.2.3", {"start": v(176.3, 25.87) * mm, "end": v(197.09, 37.88) * mm});
            skLineSegment(sketch, "E49.8.2.4", {"start": v(176.3, 1.86) * mm, "end": v(176.3, 25.87) * mm});
            skLineSegment(sketch, "E49.8.2.5", {"start": v(197.09, -10.15) * mm, "end": v(176.3, 1.86) * mm});
            skLineSegment(sketch, "E49.8.3.0", {"start": v(217.88, -78.14) * mm, "end": v(197.09, -90.15) * mm});
            skLineSegment(sketch, "E49.8.3.1", {"start": v(217.88, -54.13) * mm, "end": v(217.88, -78.14) * mm});
            skLineSegment(sketch, "E49.8.3.2", {"start": v(197.09, -42.12) * mm, "end": v(217.88, -54.13) * mm});
            skLineSegment(sketch, "E49.8.3.3", {"start": v(176.3, -54.13) * mm, "end": v(197.09, -42.12) * mm});
            skLineSegment(sketch, "E49.8.3.4", {"start": v(176.3, -78.14) * mm, "end": v(176.3, -54.13) * mm});
            skLineSegment(sketch, "E49.8.3.5", {"start": v(197.09, -90.15) * mm, "end": v(176.3, -78.14) * mm});
            skLineSegment(sketch, "E49.8.4.0", {"start": v(217.88, -158.14) * mm, "end": v(197.09, -170.15) * mm});
            skLineSegment(sketch, "E49.8.4.1", {"start": v(217.88, -134.13) * mm, "end": v(217.88, -158.14) * mm});
            skLineSegment(sketch, "E49.8.4.2", {"start": v(197.09, -122.12) * mm, "end": v(217.88, -134.13) * mm});
            skLineSegment(sketch, "E49.8.4.3", {"start": v(176.3, -134.13) * mm, "end": v(197.09, -122.12) * mm});
            skLineSegment(sketch, "E49.8.4.4", {"start": v(176.3, -158.14) * mm, "end": v(176.3, -134.13) * mm});
            skLineSegment(sketch, "E49.8.4.5", {"start": v(197.09, -170.15) * mm, "end": v(176.3, -158.14) * mm});
            skLineSegment(sketch, "E49.9.0.0", {"start": v(297.88, 161.86) * mm, "end": v(277.09, 149.85) * mm});
            skLineSegment(sketch, "E49.9.0.1", {"start": v(297.88, 185.87) * mm, "end": v(297.88, 161.86) * mm});
            skLineSegment(sketch, "E49.9.0.2", {"start": v(277.09, 197.88) * mm, "end": v(297.88, 185.87) * mm});
            skLineSegment(sketch, "E49.9.0.3", {"start": v(256.3, 185.87) * mm, "end": v(277.09, 197.88) * mm});
            skLineSegment(sketch, "E49.9.0.4", {"start": v(256.3, 161.86) * mm, "end": v(256.3, 185.87) * mm});
            skLineSegment(sketch, "E49.9.0.5", {"start": v(277.09, 149.85) * mm, "end": v(256.3, 161.86) * mm});
            skLineSegment(sketch, "E49.9.1.0", {"start": v(297.88, 81.86) * mm, "end": v(277.09, 69.85) * mm});
            skLineSegment(sketch, "E49.9.1.1", {"start": v(297.88, 105.87) * mm, "end": v(297.88, 81.86) * mm});
            skLineSegment(sketch, "E49.9.1.2", {"start": v(277.09, 117.88) * mm, "end": v(297.88, 105.87) * mm});
            skLineSegment(sketch, "E49.9.1.3", {"start": v(256.3, 105.87) * mm, "end": v(277.09, 117.88) * mm});
            skLineSegment(sketch, "E49.9.1.4", {"start": v(256.3, 81.86) * mm, "end": v(256.3, 105.87) * mm});
            skLineSegment(sketch, "E49.9.1.5", {"start": v(277.09, 69.85) * mm, "end": v(256.3, 81.86) * mm});
            skLineSegment(sketch, "E49.9.2.0", {"start": v(297.88, 1.86) * mm, "end": v(277.09, -10.15) * mm});
            skLineSegment(sketch, "E49.9.2.1", {"start": v(297.88, 25.87) * mm, "end": v(297.88, 1.86) * mm});
            skLineSegment(sketch, "E49.9.2.2", {"start": v(277.09, 37.88) * mm, "end": v(297.88, 25.87) * mm});
            skLineSegment(sketch, "E49.9.2.3", {"start": v(256.3, 25.87) * mm, "end": v(277.09, 37.88) * mm});
            skLineSegment(sketch, "E49.9.2.4", {"start": v(256.3, 1.86) * mm, "end": v(256.3, 25.87) * mm});
            skLineSegment(sketch, "E49.9.2.5", {"start": v(277.09, -10.15) * mm, "end": v(256.3, 1.86) * mm});
            skLineSegment(sketch, "E49.9.3.0", {"start": v(297.88, -78.14) * mm, "end": v(277.09, -90.15) * mm});
            skLineSegment(sketch, "E49.9.3.1", {"start": v(297.88, -54.13) * mm, "end": v(297.88, -78.14) * mm});
            skLineSegment(sketch, "E49.9.3.2", {"start": v(277.09, -42.12) * mm, "end": v(297.88, -54.13) * mm});
            skLineSegment(sketch, "E49.9.3.3", {"start": v(256.3, -54.13) * mm, "end": v(277.09, -42.12) * mm});
            skLineSegment(sketch, "E49.9.3.4", {"start": v(256.3, -78.14) * mm, "end": v(256.3, -54.13) * mm});
            skLineSegment(sketch, "E49.9.3.5", {"start": v(277.09, -90.15) * mm, "end": v(256.3, -78.14) * mm});
            skLineSegment(sketch, "E49.9.4.0", {"start": v(297.88, -158.14) * mm, "end": v(277.09, -170.15) * mm});
            skLineSegment(sketch, "E49.9.4.1", {"start": v(297.88, -134.13) * mm, "end": v(297.88, -158.14) * mm});
            skLineSegment(sketch, "E49.9.4.2", {"start": v(277.09, -122.12) * mm, "end": v(297.88, -134.13) * mm});
            skLineSegment(sketch, "E49.9.4.3", {"start": v(256.3, -134.13) * mm, "end": v(277.09, -122.12) * mm});
            skLineSegment(sketch, "E49.9.4.4", {"start": v(256.3, -158.14) * mm, "end": v(256.3, -134.13) * mm});
            skLineSegment(sketch, "E49.9.4.5", {"start": v(277.09, -170.15) * mm, "end": v(256.3, -158.14) * mm});
            skLineSegment(sketch, "E49.10.0.0", {"start": v(377.88, 161.86) * mm, "end": v(357.09, 149.85) * mm});
            skLineSegment(sketch, "E49.10.0.1", {"start": v(377.88, 185.87) * mm, "end": v(377.88, 161.86) * mm});
            skLineSegment(sketch, "E49.10.0.2", {"start": v(357.09, 197.88) * mm, "end": v(377.88, 185.87) * mm});
            skLineSegment(sketch, "E49.10.0.3", {"start": v(336.3, 185.87) * mm, "end": v(357.09, 197.88) * mm});
            skLineSegment(sketch, "E49.10.0.4", {"start": v(336.3, 161.86) * mm, "end": v(336.3, 185.87) * mm});
            skLineSegment(sketch, "E49.10.0.5", {"start": v(357.09, 149.85) * mm, "end": v(336.3, 161.86) * mm});
            skLineSegment(sketch, "E49.10.1.0", {"start": v(377.88, 81.86) * mm, "end": v(357.09, 69.85) * mm});
            skLineSegment(sketch, "E49.10.1.1", {"start": v(377.88, 105.87) * mm, "end": v(377.88, 81.86) * mm});
            skLineSegment(sketch, "E49.10.1.2", {"start": v(357.09, 117.88) * mm, "end": v(377.88, 105.87) * mm});
            skLineSegment(sketch, "E49.10.1.3", {"start": v(336.3, 105.87) * mm, "end": v(357.09, 117.88) * mm});
            skLineSegment(sketch, "E49.10.1.4", {"start": v(336.3, 81.86) * mm, "end": v(336.3, 105.87) * mm});
            skLineSegment(sketch, "E49.10.1.5", {"start": v(357.09, 69.85) * mm, "end": v(336.3, 81.86) * mm});
            skLineSegment(sketch, "E49.10.2.0", {"start": v(377.88, 1.86) * mm, "end": v(357.09, -10.15) * mm});
            skLineSegment(sketch, "E49.10.2.1", {"start": v(377.88, 25.87) * mm, "end": v(377.88, 1.86) * mm});
            skLineSegment(sketch, "E49.10.2.2", {"start": v(357.09, 37.88) * mm, "end": v(377.88, 25.87) * mm});
            skLineSegment(sketch, "E49.10.2.3", {"start": v(336.3, 25.87) * mm, "end": v(357.09, 37.88) * mm});
            skLineSegment(sketch, "E49.10.2.4", {"start": v(336.3, 1.86) * mm, "end": v(336.3, 25.87) * mm});
            skLineSegment(sketch, "E49.10.2.5", {"start": v(357.09, -10.15) * mm, "end": v(336.3, 1.86) * mm});
            skLineSegment(sketch, "E49.10.3.0", {"start": v(377.88, -78.14) * mm, "end": v(357.09, -90.15) * mm});
            skLineSegment(sketch, "E49.10.3.1", {"start": v(377.88, -54.13) * mm, "end": v(377.88, -78.14) * mm});
            skLineSegment(sketch, "E49.10.3.2", {"start": v(357.09, -42.12) * mm, "end": v(377.88, -54.13) * mm});
            skLineSegment(sketch, "E49.10.3.3", {"start": v(336.3, -54.13) * mm, "end": v(357.09, -42.12) * mm});
            skLineSegment(sketch, "E49.10.3.4", {"start": v(336.3, -78.14) * mm, "end": v(336.3, -54.13) * mm});
            skLineSegment(sketch, "E49.10.3.5", {"start": v(357.09, -90.15) * mm, "end": v(336.3, -78.14) * mm});
            skLineSegment(sketch, "E49.10.4.0", {"start": v(377.88, -158.14) * mm, "end": v(357.09, -170.15) * mm});
            skLineSegment(sketch, "E49.10.4.1", {"start": v(377.88, -134.13) * mm, "end": v(377.88, -158.14) * mm});
            skLineSegment(sketch, "E49.10.4.2", {"start": v(357.09, -122.12) * mm, "end": v(377.88, -134.13) * mm});
            skLineSegment(sketch, "E49.10.4.3", {"start": v(336.3, -134.13) * mm, "end": v(357.09, -122.12) * mm});
            skLineSegment(sketch, "E49.10.4.4", {"start": v(336.3, -158.14) * mm, "end": v(336.3, -134.13) * mm});
            skLineSegment(sketch, "E49.10.4.5", {"start": v(357.09, -170.15) * mm, "end": v(336.3, -158.14) * mm});
            skLineSegment(sketch, "E49.11.0.0", {"start": v(457.88, 161.86) * mm, "end": v(437.09, 149.85) * mm});
            skLineSegment(sketch, "E49.11.0.1", {"start": v(457.88, 185.87) * mm, "end": v(457.88, 161.86) * mm});
            skLineSegment(sketch, "E49.11.0.2", {"start": v(437.09, 197.88) * mm, "end": v(457.88, 185.87) * mm});
            skLineSegment(sketch, "E49.11.0.3", {"start": v(416.3, 185.87) * mm, "end": v(437.09, 197.88) * mm});
            skLineSegment(sketch, "E49.11.0.4", {"start": v(416.3, 161.86) * mm, "end": v(416.3, 185.87) * mm});
            skLineSegment(sketch, "E49.11.0.5", {"start": v(437.09, 149.85) * mm, "end": v(416.3, 161.86) * mm});
            skLineSegment(sketch, "E49.11.1.0", {"start": v(457.88, 81.86) * mm, "end": v(437.09, 69.85) * mm});
            skLineSegment(sketch, "E49.11.1.1", {"start": v(457.88, 105.87) * mm, "end": v(457.88, 81.86) * mm});
            skLineSegment(sketch, "E49.11.1.2", {"start": v(437.09, 117.88) * mm, "end": v(457.88, 105.87) * mm});
            skLineSegment(sketch, "E49.11.1.3", {"start": v(416.3, 105.87) * mm, "end": v(437.09, 117.88) * mm});
            skLineSegment(sketch, "E49.11.1.4", {"start": v(416.3, 81.86) * mm, "end": v(416.3, 105.87) * mm});
            skLineSegment(sketch, "E49.11.1.5", {"start": v(437.09, 69.85) * mm, "end": v(416.3, 81.86) * mm});
            skLineSegment(sketch, "E49.11.2.0", {"start": v(457.88, 1.86) * mm, "end": v(437.09, -10.15) * mm});
            skLineSegment(sketch, "E49.11.2.1", {"start": v(457.88, 25.87) * mm, "end": v(457.88, 1.86) * mm});
            skLineSegment(sketch, "E49.11.2.2", {"start": v(437.09, 37.88) * mm, "end": v(457.88, 25.87) * mm});
            skLineSegment(sketch, "E49.11.2.3", {"start": v(416.3, 25.87) * mm, "end": v(437.09, 37.88) * mm});
            skLineSegment(sketch, "E49.11.2.4", {"start": v(416.3, 1.86) * mm, "end": v(416.3, 25.87) * mm});
            skLineSegment(sketch, "E49.11.2.5", {"start": v(437.09, -10.15) * mm, "end": v(416.3, 1.86) * mm});
            skLineSegment(sketch, "E49.11.3.0", {"start": v(457.88, -78.14) * mm, "end": v(437.09, -90.15) * mm});
            skLineSegment(sketch, "E49.11.3.1", {"start": v(457.88, -54.13) * mm, "end": v(457.88, -78.14) * mm});
            skLineSegment(sketch, "E49.11.3.2", {"start": v(437.09, -42.12) * mm, "end": v(457.88, -54.13) * mm});
            skLineSegment(sketch, "E49.11.3.3", {"start": v(416.3, -54.13) * mm, "end": v(437.09, -42.12) * mm});
            skLineSegment(sketch, "E49.11.3.4", {"start": v(416.3, -78.14) * mm, "end": v(416.3, -54.13) * mm});
            skLineSegment(sketch, "E49.11.3.5", {"start": v(437.09, -90.15) * mm, "end": v(416.3, -78.14) * mm});
            skLineSegment(sketch, "E49.11.4.0", {"start": v(457.88, -158.14) * mm, "end": v(437.09, -170.15) * mm});
            skLineSegment(sketch, "E49.11.4.1", {"start": v(457.88, -134.13) * mm, "end": v(457.88, -158.14) * mm});
            skLineSegment(sketch, "E49.11.4.2", {"start": v(437.09, -122.12) * mm, "end": v(457.88, -134.13) * mm});
            skLineSegment(sketch, "E49.11.4.3", {"start": v(416.3, -134.13) * mm, "end": v(437.09, -122.12) * mm});
            skLineSegment(sketch, "E49.11.4.4", {"start": v(416.3, -158.14) * mm, "end": v(416.3, -134.13) * mm});
            skLineSegment(sketch, "E49.11.4.5", {"start": v(437.09, -170.15) * mm, "end": v(416.3, -158.14) * mm});
            skLineSegment(sketch, "E49.direction1", {"start": v(-442.91, 149.85) * mm, "end": v(-362.91, 149.85) * mm, "construction": true});
            skLineSegment(sketch, "E49.direction2", {"start": v(-442.91, 149.85) * mm, "end": v(-442.91, 69.85) * mm, "construction": true});
            skSolve(sketch);
        }
        {
            var Q0;
            Q0 = qSketchRegion(id + "F8", true);
            var Q1;
            Q1=makeQuery(id+"F2.opExtrude","CAP_FACE",FACE,{"disambiguationData":[OSD([sQuery(id+"F1.wireOp",EDGE,"E2.bottom"),sQuery(id+"F1.wireOp",EDGE,"E2.top"),sQuery(id+"F1.wireOp",EDGE,"E2.left"),sQuery(id+"F1.wireOp",EDGE,"E2.right")])],"isStart":true});
            extrude(context, id + "F9", {"entities" : qUnion([Q0]), "operationType" : NewBodyOperationType.REMOVE, "endBound" : BoundingType.UP_TO_SURFACE, "oppositeDirection" : true, "depth" : 25.4 * mm, "endBoundEntityFace" : qUnion([Q1]), "offsetDistance" : 25.4 * mm});
        }
    });
